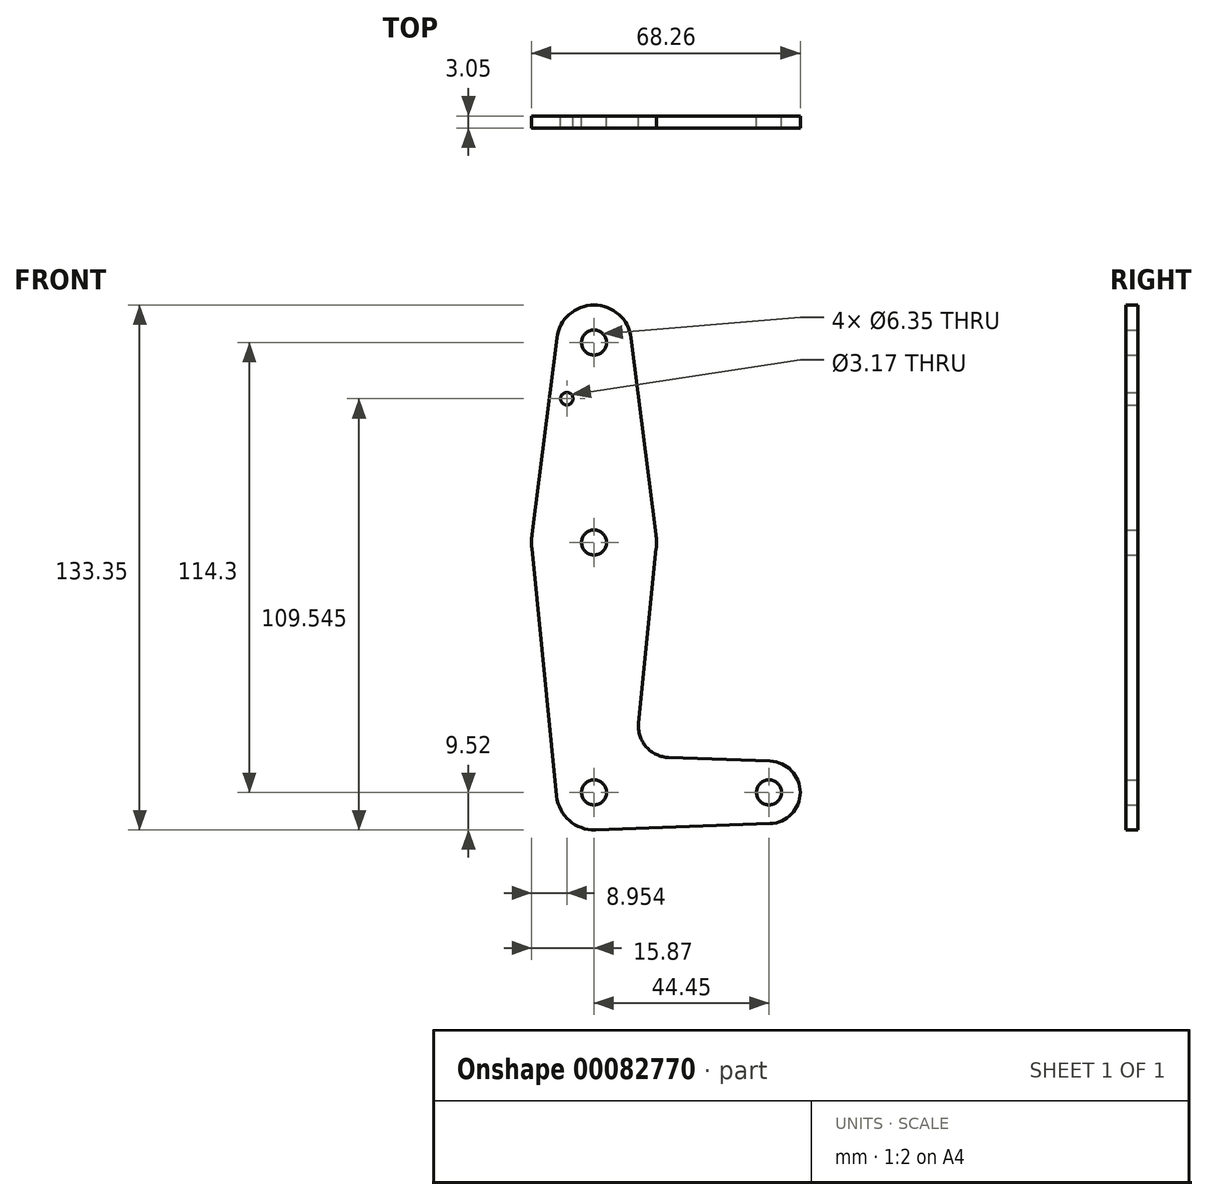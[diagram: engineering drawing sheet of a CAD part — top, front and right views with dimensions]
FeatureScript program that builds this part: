
annotation { "Feature Type Name" : "Feature", "Feature Type Description" : "" }
export const myFeature = defineFeature(function(context is Context, id is Id, definition is map)
    precondition{}
    {
        {
            var Q0;
            Q0=qCreatedBy(makeId("Front.planeOp"),FACE);
            var sketch = newSketch(context, id + "F0", { "sketchPlane" : qUnion([Q0])});
            skLineSegment(sketch, "E0", {"start": v(0, 114.3) * mm, "end": v(0, 0) * mm, "construction": true});
            skLineSegment(sketch, "E1", {"start": v(0, 0) * mm, "end": v(44.45, 0) * mm, "construction": true});
            skCircle(sketch, "E2", {"center": v(0, 114.3) * mm, "radius": 9.53 * mm});
            skCircle(sketch, "E3", {"center": v(0, 0) * mm, "radius": 9.53 * mm});
            skCircle(sketch, "E4", {"center": v(44.45, 0) * mm, "radius": 7.94 * mm});
            skCircle(sketch, "E5", {"center": v(0, 63.5) * mm, "radius": 15.88 * mm});
            skLineSegment(sketch, "E6", {"start": v(-9.45, 115.5) * mm, "end": v(-15.75, 65.48) * mm});
            skLineSegment(sketch, "E7", {"start": v(9.45, 115.5) * mm, "end": v(15.75, 65.48) * mm});
            skLineSegment(sketch, "E8", {"start": v(-15.8, 61.91) * mm, "end": v(-9.48, -0.95) * mm});
            skLineSegment(sketch, "E9", {"start": v(15.8, 61.91) * mm, "end": v(11.34, 17.6) * mm});
            skLineSegment(sketch, "E10", {"start": v(0.34, -9.52) * mm, "end": v(44.73, -7.93) * mm});
            skLineSegment(sketch, "E11", {"start": v(18.97, 8.85) * mm, "end": v(44.73, 7.93) * mm});
            skCircle(sketch, "E12", {"center": v(-6.92, 100.03) * mm, "radius": 1.59 * mm});
            skCircle(sketch, "E13", {"center": v(0, 114.3) * mm, "radius": 3.18 * mm});
            skCircle(sketch, "E14", {"center": v(0, 63.5) * mm, "radius": 3.18 * mm});
            skCircle(sketch, "E15", {"center": v(44.45, 0) * mm, "radius": 3.18 * mm});
            skCircle(sketch, "E16", {"center": v(0, 0) * mm, "radius": 3.18 * mm});
            skArc(sketch, "E17.filletArc", {"start": v(11.34, 17.6) * mm, "mid": v(13.26, 11.57) * mm, "end": v(18.97, 8.85) * mm});
            skSolve(sketch);
        }
        {
            var Q0;
            Q0 = qSketchRegion(id + "F0", true);
            extrude(context, id + "F1", {"entities" : qUnion([Q0]), "depth" : 3.05 * mm});
        }
    });
